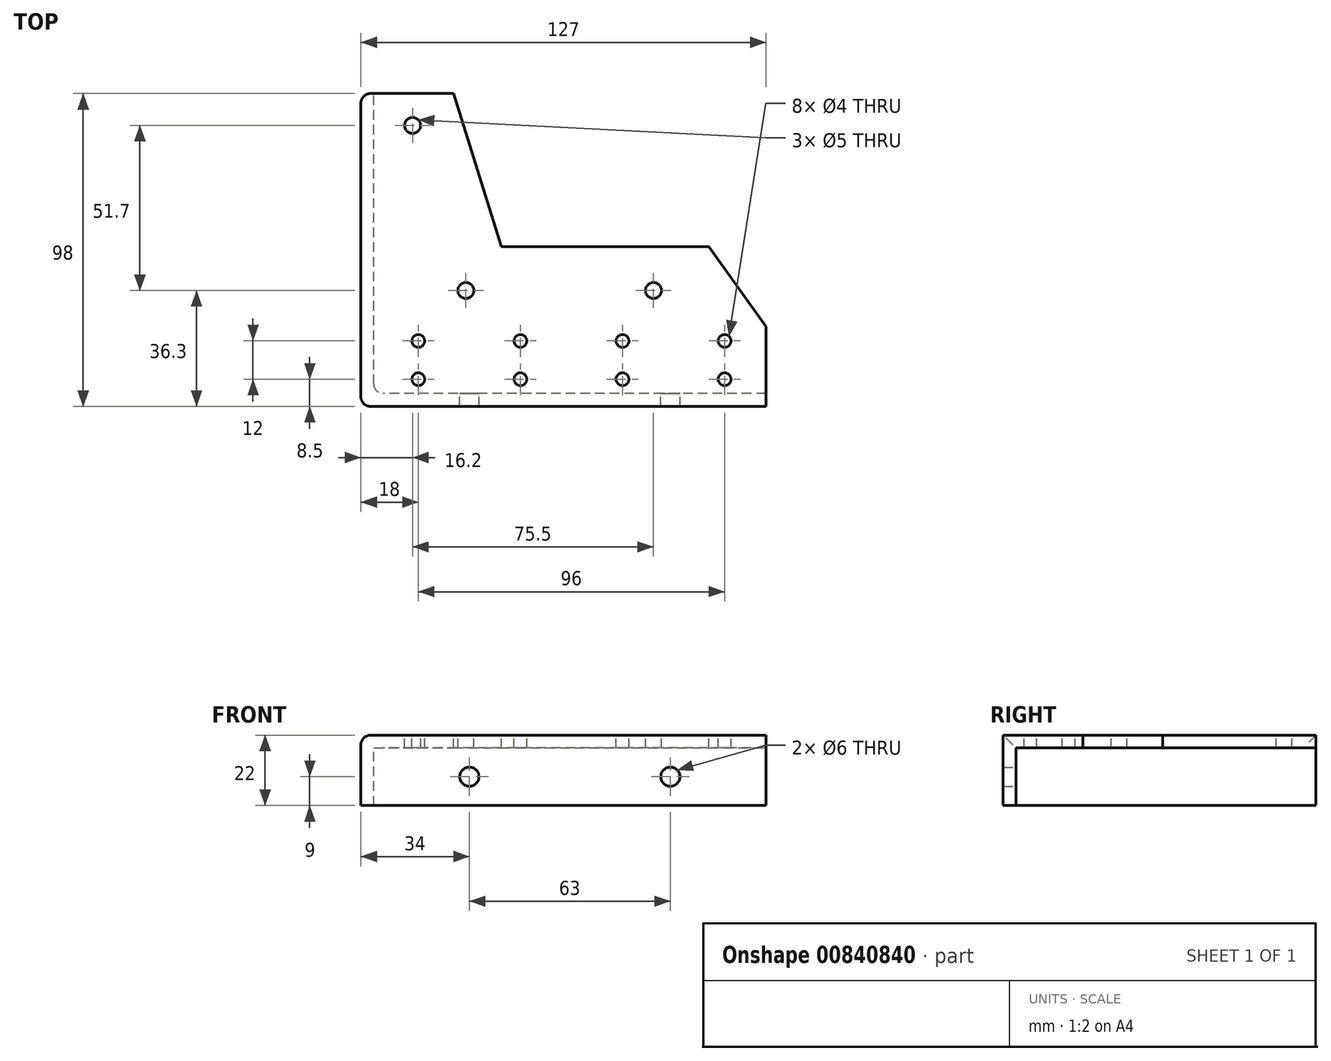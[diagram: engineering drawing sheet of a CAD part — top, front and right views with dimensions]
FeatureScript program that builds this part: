
annotation { "Feature Type Name" : "Feature", "Feature Type Description" : "" }
export const myFeature = defineFeature(function(context is Context, id is Id, definition is map)
    precondition{}
    {
        {
            var Q0;
            Q0=qCreatedBy(makeId("Top.planeOp"),FACE);
            var sketch = newSketch(context, id + "F0", { "sketchPlane" : qUnion([Q0])});
            skLineSegment(sketch, "E0.bottom", {"start": v(61.5, -10.5) * mm, "end": v(-61.5, -10.5) * mm});
            skLineSegment(sketch, "E0.top", {"start": v(61.5, 10.5) * mm, "end": v(-61.5, 10.5) * mm});
            skLineSegment(sketch, "E0.left", {"start": v(61.5, -10.5) * mm, "end": v(61.5, 10.5) * mm});
            skLineSegment(sketch, "E0.right", {"start": v(-61.5, -10.5) * mm, "end": v(-61.5, 10.5) * mm});
            skPoint(sketch, "E0.middle", {"position": v(0, 0) * mm});
            skLineSegment(sketch, "E1.bottom", {"start": v(-61.5, 10.5) * mm, "end": v(-61.5, 10.5) * mm});
            skLineSegment(sketch, "E1.top", {"start": v(-61.5, 83.5) * mm, "end": v(-61.5, 83.5) * mm});
            skLineSegment(sketch, "E1.left", {"start": v(-61.5, 10.5) * mm, "end": v(-61.5, 83.5) * mm});
            skLineSegment(sketch, "E1.right", {"start": v(-61.5, 10.5) * mm, "end": v(-61.5, 83.5) * mm});
            skLineSegment(sketch, "E2", {"start": v(-61.5, 83.5) * mm, "end": v(-36.5, 83.5) * mm});
            skLineSegment(sketch, "E3", {"start": v(-36.5, 83.5) * mm, "end": v(-21.5, 35.5) * mm});
            skLineSegment(sketch, "E4", {"start": v(-21.5, 35.5) * mm, "end": v(43.5, 35.5) * mm});
            skLineSegment(sketch, "E5", {"start": v(43.5, 35.5) * mm, "end": v(61.5, 10.5) * mm});
            skLineSegment(sketch, "E6.bottom", {"start": v(-61.5, -10.5) * mm, "end": v(61.5, -10.5) * mm});
            skLineSegment(sketch, "E6.top", {"start": v(-61.5, -14.5) * mm, "end": v(61.5, -14.5) * mm});
            skLineSegment(sketch, "E6.left", {"start": v(-61.5, -10.5) * mm, "end": v(-61.5, -14.5) * mm});
            skLineSegment(sketch, "E6.right", {"start": v(61.5, -10.5) * mm, "end": v(61.5, -14.5) * mm});
            skLineSegment(sketch, "E7.bottom", {"start": v(-61.5, -14.5) * mm, "end": v(-65.5, -14.5) * mm});
            skLineSegment(sketch, "E7.top", {"start": v(-61.5, 83.5) * mm, "end": v(-65.5, 83.5) * mm});
            skLineSegment(sketch, "E7.left", {"start": v(-61.5, -14.5) * mm, "end": v(-61.5, 83.5) * mm});
            skLineSegment(sketch, "E7.right", {"start": v(-65.5, -14.5) * mm, "end": v(-65.5, 83.5) * mm});
            skLineSegment(sketch, "E8", {"start": v(-61.5, 73.5) * mm, "end": v(-49.3, 73.5) * mm, "construction": true});
            skLineSegment(sketch, "E9", {"start": v(-61.5, 21.8) * mm, "end": v(-32.6, 21.8) * mm, "construction": true});
            skLineSegment(sketch, "E10", {"start": v(26.2, 10.5) * mm, "end": v(26.2, 21.8) * mm, "construction": true});
            skLineSegment(sketch, "E11", {"start": v(61.5, -10.5) * mm, "end": v(61.5, 6) * mm, "construction": true});
            skLineSegment(sketch, "E12", {"start": v(61.5, 6) * mm, "end": v(48.5, 6) * mm, "construction": true});
            skLineSegment(sketch, "E13", {"start": v(48.5, 6) * mm, "end": v(16.5, 6) * mm, "construction": true});
            skLineSegment(sketch, "E14", {"start": v(16.5, 6) * mm, "end": v(-15.5, 6) * mm, "construction": true});
            skLineSegment(sketch, "E15", {"start": v(-15.5, 6) * mm, "end": v(-47.5, 6) * mm, "construction": true});
            skLineSegment(sketch, "E16", {"start": v(-47.5, 6) * mm, "end": v(-61.5, 6) * mm, "construction": true});
            skLineSegment(sketch, "E17", {"start": v(61.5, 6) * mm, "end": v(61.5, -6) * mm, "construction": true});
            skLineSegment(sketch, "E18", {"start": v(61.5, -6) * mm, "end": v(48.5, -6) * mm, "construction": true});
            skLineSegment(sketch, "E19", {"start": v(48.5, -6) * mm, "end": v(16.5, -6) * mm, "construction": true});
            skLineSegment(sketch, "E20", {"start": v(16.5, -6) * mm, "end": v(-15.5, -6) * mm, "construction": true});
            skLineSegment(sketch, "E21", {"start": v(-15.5, -6) * mm, "end": v(-47.5, -6) * mm, "construction": true});
            skLineSegment(sketch, "E22", {"start": v(-47.5, -6) * mm, "end": v(-61.5, -6) * mm, "construction": true});
            skSolve(sketch);
        }
        {
            var Q0;
            Q0=makeQuery(id+"F0.imprint","IMPRINT",FACE,{"disambiguationData":[TD([[makeQuery(id+"F0.imprint","IMPRINT",EDGE,{"derivedFrom":sQuery(id+"F0.wireOp",EDGE,"E0.bottom")}),-1.0]])]});
            var Q1;
            Q1=makeQuery(id+"F0.imprint","IMPRINT",FACE,{"disambiguationData":[TD([[makeQuery(id+"F0.imprint","IMPRINT",EDGE,{"derivedFrom":sQuery(id+"F0.wireOp",EDGE,"E0.top")}),-1.0]])]});
            extrude(context, id + "F1", {"entities" : qUnion([Q0, Q1]), "oppositeDirection" : true, "depth" : 4 * mm, "offsetDistance" : 25 * mm});
        }
        {
            var Q0;
            Q0=makeQuery(id+"F0.imprint","IMPRINT",FACE,{"disambiguationData":[TD([[makeQuery(id+"F0.imprint","IMPRINT",EDGE,{"derivedFrom":sQuery(id+"F0.wireOp",EDGE,"E0.right")}),1.0]])]});
            var Q1;
            Q1=makeQuery(id+"F0.imprint","IMPRINT",FACE,{"disambiguationData":[TD([[makeQuery(id+"F0.imprint","IMPRINT",EDGE,{"derivedFrom":sQuery(id+"F0.wireOp",EDGE,"E0.bottom")}),1.0]])]});
            extrude(context, id + "F2", {"entities" : qUnion([Q0, Q1]), "operationType" : NewBodyOperationType.ADD, "oppositeDirection" : true, "depth" : 22 * mm, "offsetDistance" : 25 * mm});
        }
        {
            var Q0;
            Q0=sQuery(id+"F0.wireOp",VERTEX,"E8.end");
            var Q1;
            Q1=sQuery(id+"F0.wireOp",VERTEX,"E9.end");
            var Q2;
            Q2=sQuery(id+"F0.wireOp",VERTEX,"E10.end");
            var Q3;
            Q3=makeQuery(id+"F1.opExtrude","SWEPT_BODY",BODY,{"disambiguationData":[OSD([sQuery(id+"F0.wireOp",EDGE,"E0.bottom"),sQuery(id+"F0.wireOp",EDGE,"E0.left"),sQuery(id+"F0.wireOp",EDGE,"E0.right"),sQuery(id+"F0.wireOp",EDGE,"E1.left"),sQuery(id+"F0.wireOp",EDGE,"E2"),sQuery(id+"F0.wireOp",EDGE,"E3"),sQuery(id+"F0.wireOp",EDGE,"E4"),sQuery(id+"F0.wireOp",EDGE,"E5")])]});
            hole(context, id + "F3", {"style" : HoleStyle.SIMPLE, "endStyle" : HoleEndStyle.THROUGH, "holeDiameter" : 5 * mm, "majorDiameter" : 5 * mm, "isTappedThrough" : true, "tappedDepth" : 12 * mm, "tapClearance" : 3, "locations" : qUnion([Q0, Q1, Q2]), "scope" : qUnion([Q3])});
        }
        {
            var Q0;
            Q0=sQuery(id+"F0.wireOp",VERTEX,"E15.end");
            var Q1;
            Q1=sQuery(id+"F0.wireOp",VERTEX,"E21.end");
            var Q2;
            Q2=sQuery(id+"F0.wireOp",VERTEX,"E20.end");
            var Q3;
            Q3=sQuery(id+"F0.wireOp",VERTEX,"E14.end");
            var Q4;
            Q4=sQuery(id+"F0.wireOp",VERTEX,"E19.end");
            var Q5;
            Q5=sQuery(id+"F0.wireOp",VERTEX,"E13.end");
            var Q6;
            Q6=sQuery(id+"F0.wireOp",VERTEX,"E12.end");
            var Q7;
            Q7=sQuery(id+"F0.wireOp",VERTEX,"E18.end");
            var Q8;
            Q8=makeQuery(id+"F1.opExtrude","SWEPT_BODY",BODY,{"disambiguationData":[OSD([sQuery(id+"F0.wireOp",EDGE,"E0.bottom"),sQuery(id+"F0.wireOp",EDGE,"E0.left"),sQuery(id+"F0.wireOp",EDGE,"E0.right"),sQuery(id+"F0.wireOp",EDGE,"E1.left"),sQuery(id+"F0.wireOp",EDGE,"E2"),sQuery(id+"F0.wireOp",EDGE,"E3"),sQuery(id+"F0.wireOp",EDGE,"E4"),sQuery(id+"F0.wireOp",EDGE,"E5")])]});
            hole(context, id + "F4", {"style" : HoleStyle.SIMPLE, "endStyle" : HoleEndStyle.THROUGH, "holeDiameter" : 4 * mm, "majorDiameter" : 5 * mm, "isTappedThrough" : true, "tappedDepth" : 12 * mm, "tapClearance" : 3, "locations" : qUnion([Q0, Q1, Q2, Q3, Q4, Q5, Q6, Q7]), "scope" : qUnion([Q8])});
        }
        {
            var Q0;
            Q0=makeQuery(id+"F2.opExtrude","SWEPT_FACE",FACE,{"disambiguationData":[OSD([sQuery(id+"F0.wireOp",EDGE,"E0.bottom")])]});
            var sketch = newSketch(context, id + "F5", { "sketchPlane" : qUnion([Q0])});
            skLineSegment(sketch, "E23", {"start": v(-61.5, -13) * mm, "end": v(-31.5, -13) * mm, "construction": true});
            skLineSegment(sketch, "E24", {"start": v(-31.5, -13) * mm, "end": v(31.5, -13) * mm, "construction": true});
            skLineSegment(sketch, "E25", {"start": v(31.5, -13) * mm, "end": v(61.5, -13) * mm, "construction": true});
            skSolve(sketch);
        }
        {
            var Q0;
            Q0=sQuery(id+"F5.wireOp",VERTEX,"E23.end");
            var Q1;
            Q1=sQuery(id+"F5.wireOp",VERTEX,"E24.end");
            var Q2;
            Q2=makeQuery(id+"F1.opExtrude","SWEPT_BODY",BODY,{"disambiguationData":[OSD([sQuery(id+"F0.wireOp",EDGE,"E0.bottom"),sQuery(id+"F0.wireOp",EDGE,"E0.left"),sQuery(id+"F0.wireOp",EDGE,"E0.right"),sQuery(id+"F0.wireOp",EDGE,"E1.left"),sQuery(id+"F0.wireOp",EDGE,"E2"),sQuery(id+"F0.wireOp",EDGE,"E3"),sQuery(id+"F0.wireOp",EDGE,"E4"),sQuery(id+"F0.wireOp",EDGE,"E5")])]});
            hole(context, id + "F6", {"style" : HoleStyle.SIMPLE, "endStyle" : HoleEndStyle.THROUGH, "holeDiameter" : 6 * mm, "majorDiameter" : 5 * mm, "isTappedThrough" : true, "tappedDepth" : 12 * mm, "tapClearance" : 3, "locations" : qUnion([Q0, Q1]), "scope" : qUnion([Q2])});
        }
        {
            var Q0;
            Q0=makeQuery(id+"F1.opExtrude","CAP_EDGE",EDGE,{"disambiguationData":[OSD([sQuery(id+"F0.wireOp",EDGE,"E0.bottom")])],"isStart":false});
            var Q1;
            Q1=makeQuery(id+"F1.opExtrude","CAP_EDGE",EDGE,{"disambiguationData":[OSD([sQuery(id+"F0.wireOp",EDGE,"E0.right"),sQuery(id+"F0.wireOp",EDGE,"E1.left")])],"isStart":false});
            var Q2;
            Q2=makeQuery(id+"F2.opExtrude","SWEPT_EDGE",EDGE,{"disambiguationData":[OSD([sQuery(id+"F0.wireOp",EDGE,"E0.bottom"),sQuery(id+"F0.wireOp",EDGE,"E0.right"),sQuery(id+"F0.wireOp",EDGE,"E6.left")])]});
            var Q3;
            Q3=makeQuery(id+"F2.opExtrude","SWEPT_EDGE",EDGE,{"disambiguationData":[OSD([sQuery(id+"F0.wireOp",EDGE,"E7.bottom"),sQuery(id+"F0.wireOp",EDGE,"E7.right")])]});
            var Q4;
            Q4=makeQuery(id+"F2.opExtrude","CAP_EDGE",EDGE,{"disambiguationData":[OSD([sQuery(id+"F0.wireOp",EDGE,"E7.right")])],"isStart":true});
            var Q5;
            Q5=makeQuery(id+"F2.opExtrude","SWEPT_EDGE",EDGE,{"disambiguationData":[OSD([sQuery(id+"F0.wireOp",EDGE,"E7.top"),sQuery(id+"F0.wireOp",EDGE,"E7.right")])]});
            fillet(context, id + "F7", {"entities" : qUnion([Q0, Q1, Q2, Q3, Q4, Q5]), "radius" : 3 * mm, "tangentPropagation" : true, "allowEdgeOverflow" : false});
        }
    });
